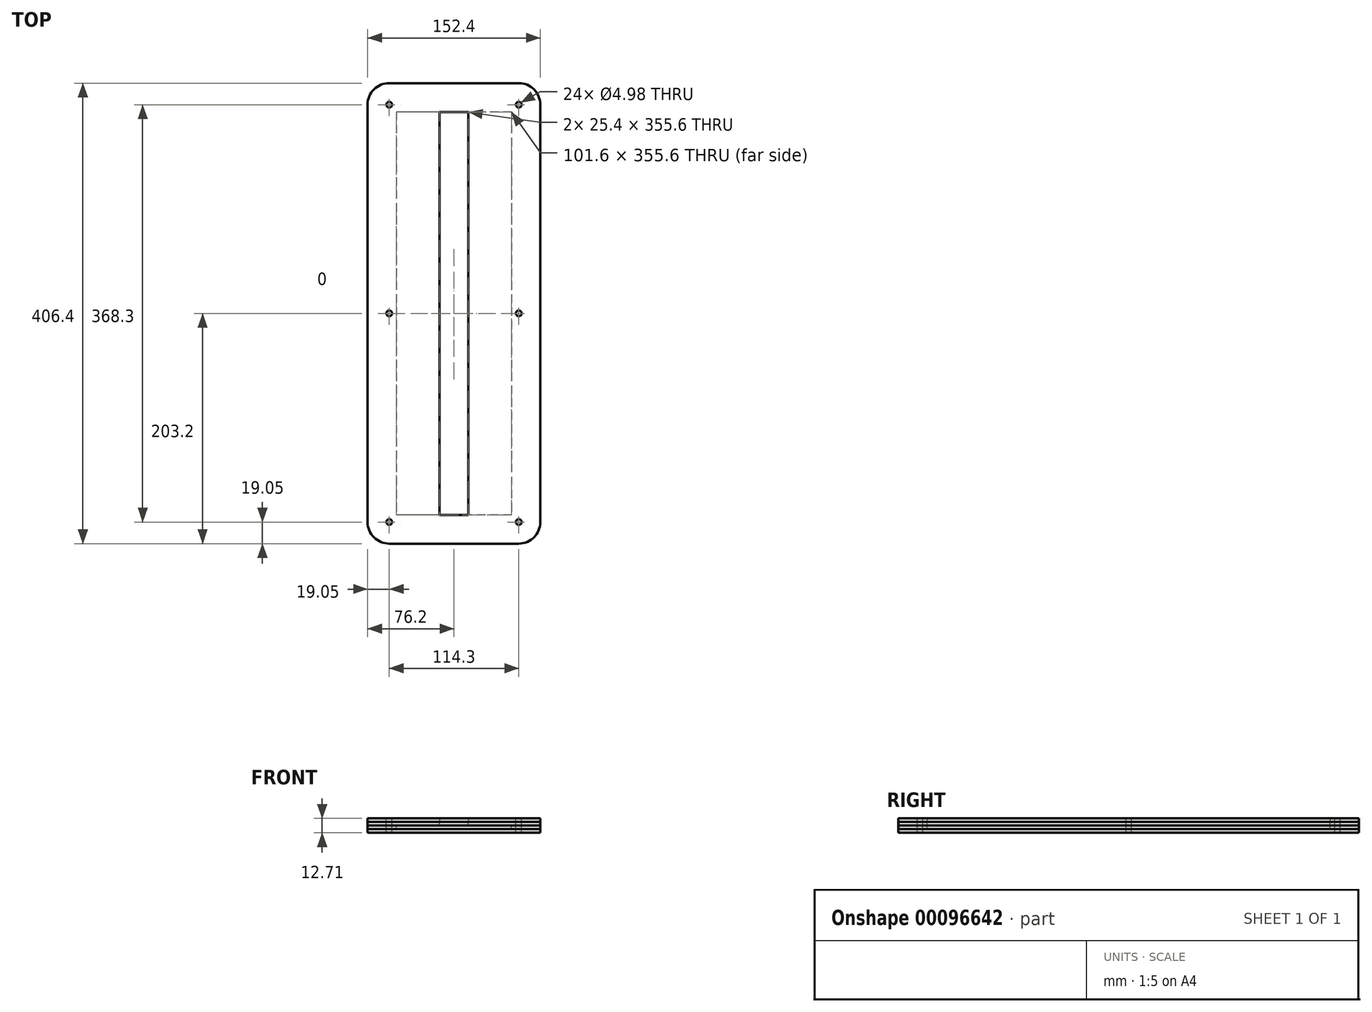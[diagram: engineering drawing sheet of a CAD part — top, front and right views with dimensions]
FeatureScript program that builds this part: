
annotation { "Feature Type Name" : "Feature", "Feature Type Description" : "" }
export const myFeature = defineFeature(function(context is Context, id is Id, definition is map)
    precondition{}
    {
        {
            var Q0;
            Q0=qCreatedBy(makeId("Top.planeOp"),FACE);
            var sketch = newSketch(context, id + "F0", { "sketchPlane" : qUnion([Q0])});
            skLineSegment(sketch, "E0.bottom", {"start": v(76.2, 203.2) * mm, "end": v(-76.2, 203.2) * mm});
            skLineSegment(sketch, "E0.top", {"start": v(76.2, -203.2) * mm, "end": v(-76.2, -203.2) * mm});
            skLineSegment(sketch, "E0.left", {"start": v(76.2, 203.2) * mm, "end": v(76.2, -203.2) * mm});
            skLineSegment(sketch, "E0.right", {"start": v(-76.2, 203.2) * mm, "end": v(-76.2, -203.2) * mm});
            skPoint(sketch, "E0.middle", {"position": v(0, 0) * mm});
            skLineSegment(sketch, "E1.bottom", {"start": v(12.7, 177.8) * mm, "end": v(-12.7, 177.8) * mm});
            skLineSegment(sketch, "E1.top", {"start": v(12.7, -177.8) * mm, "end": v(-12.7, -177.8) * mm});
            skLineSegment(sketch, "E1.left", {"start": v(12.7, 177.8) * mm, "end": v(12.7, -177.8) * mm});
            skLineSegment(sketch, "E1.right", {"start": v(-12.7, 177.8) * mm, "end": v(-12.7, -177.8) * mm});
            skSolve(sketch);
        }
        {
            var Q0;
            Q0 = qSketchRegion(id + "F0", true);
            extrude(context, id + "F1", {"entities" : qUnion([Q0]), "depth" : 3.17 * mm});
        }
        {
            var Q0;
            Q0=makeQuery(id+"F1.opExtrude","CAP_FACE",FACE,{"disambiguationData":[OSD([sQuery(id+"F0.wireOp",EDGE,"E0.bottom"),sQuery(id+"F0.wireOp",EDGE,"E0.top"),sQuery(id+"F0.wireOp",EDGE,"E0.left"),sQuery(id+"F0.wireOp",EDGE,"E0.right")])],"isStart":true});
            var sketch = newSketch(context, id + "F2", { "sketchPlane" : qUnion([Q0])});
            skLineSegment(sketch, "E2.bottom", {"start": v(76.2, 203.2) * mm, "end": v(-76.2, 203.2) * mm});
            skLineSegment(sketch, "E2.top", {"start": v(76.2, -203.2) * mm, "end": v(-76.2, -203.2) * mm});
            skLineSegment(sketch, "E2.left", {"start": v(76.2, 203.2) * mm, "end": v(76.2, -203.2) * mm});
            skLineSegment(sketch, "E2.right", {"start": v(-76.2, 203.2) * mm, "end": v(-76.2, -203.2) * mm});
            skPoint(sketch, "E2.middle", {"position": v(0, 0) * mm});
            skLineSegment(sketch, "E3.bottom", {"start": v(12.7, 177.8) * mm, "end": v(-12.7, 177.8) * mm});
            skLineSegment(sketch, "E3.top", {"start": v(12.7, -177.8) * mm, "end": v(-12.7, -177.8) * mm});
            skLineSegment(sketch, "E3.left", {"start": v(12.7, 177.8) * mm, "end": v(12.7, -177.8) * mm});
            skLineSegment(sketch, "E3.right", {"start": v(-12.7, 177.8) * mm, "end": v(-12.7, -177.8) * mm});
            skSolve(sketch);
        }
        {
            var Q0;
            Q0 = qSketchRegion(id + "F2", true);
            extrude(context, id + "F3", {"entities" : qUnion([Q0]), "depth" : 3.17 * mm});
        }
        {
            var Q0;
            Q0=makeQuery(id+"F3.opExtrude","CAP_FACE",FACE,{"disambiguationData":[OSD([sQuery(id+"F2.wireOp",EDGE,"E2.bottom"),sQuery(id+"F2.wireOp",EDGE,"E2.top"),sQuery(id+"F2.wireOp",EDGE,"E2.left"),sQuery(id+"F2.wireOp",EDGE,"E2.right"),sQuery(id+"F2.wireOp",EDGE,"E3.bottom"),sQuery(id+"F2.wireOp",EDGE,"E3.top"),sQuery(id+"F2.wireOp",EDGE,"E3.left"),sQuery(id+"F2.wireOp",EDGE,"E3.right")])],"isStart":false});
            var sketch = newSketch(context, id + "F4", { "sketchPlane" : qUnion([Q0])});
            skLineSegment(sketch, "E4.bottom", {"start": v(76.2, -203.2) * mm, "end": v(-76.2, -203.2) * mm});
            skLineSegment(sketch, "E4.top", {"start": v(76.2, 203.2) * mm, "end": v(-76.2, 203.2) * mm});
            skLineSegment(sketch, "E4.left", {"start": v(76.2, -203.2) * mm, "end": v(76.2, 203.2) * mm});
            skLineSegment(sketch, "E4.right", {"start": v(-76.2, -203.2) * mm, "end": v(-76.2, 203.2) * mm});
            skPoint(sketch, "E4.middle", {"position": v(0, 0) * mm});
            skLineSegment(sketch, "E5.bottom", {"start": v(50.8, -177.8) * mm, "end": v(-50.8, -177.8) * mm});
            skLineSegment(sketch, "E5.top", {"start": v(50.8, 177.8) * mm, "end": v(-50.8, 177.8) * mm});
            skLineSegment(sketch, "E5.left", {"start": v(50.8, -177.8) * mm, "end": v(50.8, 177.8) * mm});
            skLineSegment(sketch, "E5.right", {"start": v(-50.8, -177.8) * mm, "end": v(-50.8, 177.8) * mm});
            skSolve(sketch);
        }
        {
            var Q0;
            Q0 = qSketchRegion(id + "F4", true);
            extrude(context, id + "F5", {"entities" : qUnion([Q0]), "depth" : 3.17 * mm});
        }
        {
            var Q0;
            Q0=makeQuery(id+"F5.opExtrude","CAP_FACE",FACE,{"disambiguationData":[OSD([sQuery(id+"F4.wireOp",EDGE,"E4.bottom"),sQuery(id+"F4.wireOp",EDGE,"E4.top"),sQuery(id+"F4.wireOp",EDGE,"E4.left"),sQuery(id+"F4.wireOp",EDGE,"E4.right"),sQuery(id+"F4.wireOp",EDGE,"E5.bottom"),sQuery(id+"F4.wireOp",EDGE,"E5.top"),sQuery(id+"F4.wireOp",EDGE,"E5.left"),sQuery(id+"F4.wireOp",EDGE,"E5.right")])],"isStart":false});
            var sketch = newSketch(context, id + "F6", { "sketchPlane" : qUnion([Q0])});
            skLineSegment(sketch, "E6.bottom", {"start": v(76.2, -203.2) * mm, "end": v(-76.2, -203.2) * mm});
            skLineSegment(sketch, "E6.top", {"start": v(76.2, 203.2) * mm, "end": v(-76.2, 203.2) * mm});
            skLineSegment(sketch, "E6.left", {"start": v(76.2, 203.2) * mm, "end": v(76.2, -203.2) * mm});
            skLineSegment(sketch, "E6.right", {"start": v(-76.2, 203.2) * mm, "end": v(-76.2, -203.2) * mm});
            skPoint(sketch, "E6.middle", {"position": v(0, 0) * mm});
            skSolve(sketch);
        }
        {
            var Q0;
            Q0 = qSketchRegion(id + "F6", true);
            extrude(context, id + "F7", {"entities" : qUnion([Q0]), "depth" : 3.17 * mm});
        }
        {
            var Q0;
            Q0=makeQuery(id+"F1.opExtrude","CAP_FACE",FACE,{"disambiguationData":[OSD([sQuery(id+"F0.wireOp",EDGE,"E0.bottom"),sQuery(id+"F0.wireOp",EDGE,"E0.top"),sQuery(id+"F0.wireOp",EDGE,"E0.left"),sQuery(id+"F0.wireOp",EDGE,"E0.right"),sQuery(id+"F0.wireOp",EDGE,"E1.bottom"),sQuery(id+"F0.wireOp",EDGE,"E1.top"),sQuery(id+"F0.wireOp",EDGE,"E1.left"),sQuery(id+"F0.wireOp",EDGE,"E1.right")])],"isStart":false});
            var sketch = newSketch(context, id + "F8", { "sketchPlane" : qUnion([Q0])});
            skPoint(sketch, "E7", {"position": v(-57.15, 184.15) * mm});
            skPoint(sketch, "E8.0.1.0", {"position": v(-57.15, 0) * mm});
            skPoint(sketch, "E8.0.2.0", {"position": v(-57.15, -184.15) * mm});
            skPoint(sketch, "E8.1.0.0", {"position": v(57.15, 184.15) * mm});
            skPoint(sketch, "E8.1.1.0", {"position": v(57.15, 0) * mm});
            skPoint(sketch, "E8.1.2.0", {"position": v(57.15, -184.15) * mm});
            skLineSegment(sketch, "E8.direction1", {"start": v(-57.15, 184.15) * mm, "end": v(57.15, 184.15) * mm, "construction": true});
            skLineSegment(sketch, "E8.direction2", {"start": v(-57.15, 184.15) * mm, "end": v(-57.15, 0) * mm, "construction": true});
            skSolve(sketch);
        }
        {
            var Q0;
            Q0=makeQuery(id+"F1.opExtrude","SWEPT_EDGE",EDGE,{"disambiguationData":[OSD([sQuery(id+"F0.wireOp",EDGE,"E0.top"),sQuery(id+"F0.wireOp",EDGE,"E0.right")])]});
            var Q1;
            Q1=makeQuery(id+"F3.opExtrude","SWEPT_EDGE",EDGE,{"disambiguationData":[OSD([sQuery(id+"F2.wireOp",EDGE,"E2.bottom"),sQuery(id+"F2.wireOp",EDGE,"E2.right")])]});
            var Q2;
            Q2=makeQuery(id+"F5.opExtrude","SWEPT_EDGE",EDGE,{"disambiguationData":[OSD([sQuery(id+"F4.wireOp",EDGE,"E4.top"),sQuery(id+"F4.wireOp",EDGE,"E4.right")])]});
            var Q3;
            Q3=makeQuery(id+"F7.opExtrude","SWEPT_EDGE",EDGE,{"disambiguationData":[OSD([sQuery(id+"F6.wireOp",EDGE,"E6.top"),sQuery(id+"F6.wireOp",EDGE,"E6.right")])]});
            var Q4;
            Q4=makeQuery(id+"F1.opExtrude","SWEPT_EDGE",EDGE,{"disambiguationData":[OSD([sQuery(id+"F0.wireOp",EDGE,"E0.top"),sQuery(id+"F0.wireOp",EDGE,"E0.left")])]});
            var Q5;
            Q5=makeQuery(id+"F3.opExtrude","SWEPT_EDGE",EDGE,{"disambiguationData":[OSD([sQuery(id+"F2.wireOp",EDGE,"E2.bottom"),sQuery(id+"F2.wireOp",EDGE,"E2.left")])]});
            var Q6;
            Q6=makeQuery(id+"F5.opExtrude","SWEPT_EDGE",EDGE,{"disambiguationData":[OSD([sQuery(id+"F4.wireOp",EDGE,"E4.top"),sQuery(id+"F4.wireOp",EDGE,"E4.left")])]});
            var Q7;
            Q7=makeQuery(id+"F7.opExtrude","SWEPT_EDGE",EDGE,{"disambiguationData":[OSD([sQuery(id+"F6.wireOp",EDGE,"E6.top"),sQuery(id+"F6.wireOp",EDGE,"E6.left")])]});
            var Q8;
            Q8=makeQuery(id+"F1.opExtrude","SWEPT_EDGE",EDGE,{"disambiguationData":[OSD([sQuery(id+"F0.wireOp",EDGE,"E0.bottom"),sQuery(id+"F0.wireOp",EDGE,"E0.left")])]});
            var Q9;
            Q9=makeQuery(id+"F3.opExtrude","SWEPT_EDGE",EDGE,{"disambiguationData":[OSD([sQuery(id+"F2.wireOp",EDGE,"E2.top"),sQuery(id+"F2.wireOp",EDGE,"E2.left")])]});
            var Q10;
            Q10=makeQuery(id+"F5.opExtrude","SWEPT_EDGE",EDGE,{"disambiguationData":[OSD([sQuery(id+"F4.wireOp",EDGE,"E4.bottom"),sQuery(id+"F4.wireOp",EDGE,"E4.left")])]});
            var Q11;
            Q11=makeQuery(id+"F7.opExtrude","SWEPT_EDGE",EDGE,{"disambiguationData":[OSD([sQuery(id+"F6.wireOp",EDGE,"E6.bottom"),sQuery(id+"F6.wireOp",EDGE,"E6.left")])]});
            var Q12;
            Q12=makeQuery(id+"F1.opExtrude","SWEPT_EDGE",EDGE,{"disambiguationData":[OSD([sQuery(id+"F0.wireOp",EDGE,"E0.bottom"),sQuery(id+"F0.wireOp",EDGE,"E0.right")])]});
            var Q13;
            Q13=makeQuery(id+"F3.opExtrude","SWEPT_EDGE",EDGE,{"disambiguationData":[OSD([sQuery(id+"F2.wireOp",EDGE,"E2.top"),sQuery(id+"F2.wireOp",EDGE,"E2.right")])]});
            var Q14;
            Q14=makeQuery(id+"F5.opExtrude","SWEPT_EDGE",EDGE,{"disambiguationData":[OSD([sQuery(id+"F4.wireOp",EDGE,"E4.bottom"),sQuery(id+"F4.wireOp",EDGE,"E4.right")])]});
            var Q15;
            Q15=makeQuery(id+"F7.opExtrude","SWEPT_EDGE",EDGE,{"disambiguationData":[OSD([sQuery(id+"F6.wireOp",EDGE,"E6.bottom"),sQuery(id+"F6.wireOp",EDGE,"E6.right")])]});
            fillet(context, id + "F9", {"entities" : qUnion([Q0, Q1, Q2, Q3, Q4, Q5, Q6, Q7, Q8, Q9, Q10, Q11, Q12, Q13, Q14, Q15]), "radius" : 19.05 * mm, "tangentPropagation" : true, "allowEdgeOverflow" : false});
        }
        {
            var Q0;
            Q0=sQuery(id+"F8.wireOp",VERTEX,"E7");
            var Q1;
            Q1=sQuery(id+"F8.wireOp",VERTEX,"E8.1.0.0");
            var Q2;
            Q2=sQuery(id+"F8.wireOp",VERTEX,"E8.1.1.0");
            var Q3;
            Q3=sQuery(id+"F8.wireOp",VERTEX,"E8.0.1.0");
            var Q4;
            Q4=sQuery(id+"F8.wireOp",VERTEX,"E8.0.2.0");
            var Q5;
            Q5=sQuery(id+"F8.wireOp",VERTEX,"E8.1.2.0");
            var Q6;
            Q6=makeQuery(id+"F7.opExtrude","SWEPT_BODY",BODY,{"disambiguationData":[OSD([sQuery(id+"F6.wireOp",EDGE,"E6.bottom"),sQuery(id+"F6.wireOp",EDGE,"E6.top"),sQuery(id+"F6.wireOp",EDGE,"E6.left"),sQuery(id+"F6.wireOp",EDGE,"E6.right")])]});
            var Q7;
            Q7=makeQuery(id+"F1.opExtrude","SWEPT_BODY",BODY,{"disambiguationData":[OSD([sQuery(id+"F0.wireOp",EDGE,"E0.bottom"),sQuery(id+"F0.wireOp",EDGE,"E0.top"),sQuery(id+"F0.wireOp",EDGE,"E0.left"),sQuery(id+"F0.wireOp",EDGE,"E0.right"),sQuery(id+"F0.wireOp",EDGE,"E1.bottom"),sQuery(id+"F0.wireOp",EDGE,"E1.top"),sQuery(id+"F0.wireOp",EDGE,"E1.left"),sQuery(id+"F0.wireOp",EDGE,"E1.right")])]});
            var Q8;
            Q8=makeQuery(id+"F3.opExtrude","SWEPT_BODY",BODY,{"disambiguationData":[OSD([sQuery(id+"F2.wireOp",EDGE,"E2.bottom"),sQuery(id+"F2.wireOp",EDGE,"E2.top"),sQuery(id+"F2.wireOp",EDGE,"E2.left"),sQuery(id+"F2.wireOp",EDGE,"E2.right"),sQuery(id+"F2.wireOp",EDGE,"E3.bottom"),sQuery(id+"F2.wireOp",EDGE,"E3.top"),sQuery(id+"F2.wireOp",EDGE,"E3.left"),sQuery(id+"F2.wireOp",EDGE,"E3.right")])]});
            var Q9;
            Q9=makeQuery(id+"F5.opExtrude","SWEPT_BODY",BODY,{"disambiguationData":[OSD([sQuery(id+"F4.wireOp",EDGE,"E4.bottom"),sQuery(id+"F4.wireOp",EDGE,"E4.top"),sQuery(id+"F4.wireOp",EDGE,"E4.left"),sQuery(id+"F4.wireOp",EDGE,"E4.right"),sQuery(id+"F4.wireOp",EDGE,"E5.bottom"),sQuery(id+"F4.wireOp",EDGE,"E5.top"),sQuery(id+"F4.wireOp",EDGE,"E5.left"),sQuery(id+"F4.wireOp",EDGE,"E5.right")])]});
            hole(context, id + "F10", {"style" : HoleStyle.SIMPLE, "endStyle" : HoleEndStyle.THROUGH, "standardTappedOrClearance" : lookupTablePath({ "standard" : "ANSI", "fit" : "Close", "size" : "#10", "type" : "Clearance" }), "standardBlindInLast" : lookupTablePath({ "fit" : "Close", "standard" : "ANSI", "size" : "#10", "type" : "Clearance" }), "holeDiameter" : 4.98 * mm, "locations" : qUnion([Q0, Q1, Q2, Q3, Q4, Q5]), "scope" : qUnion([Q6, Q7, Q8, Q9]), "isTappedThrough" : true});
        }
    });
